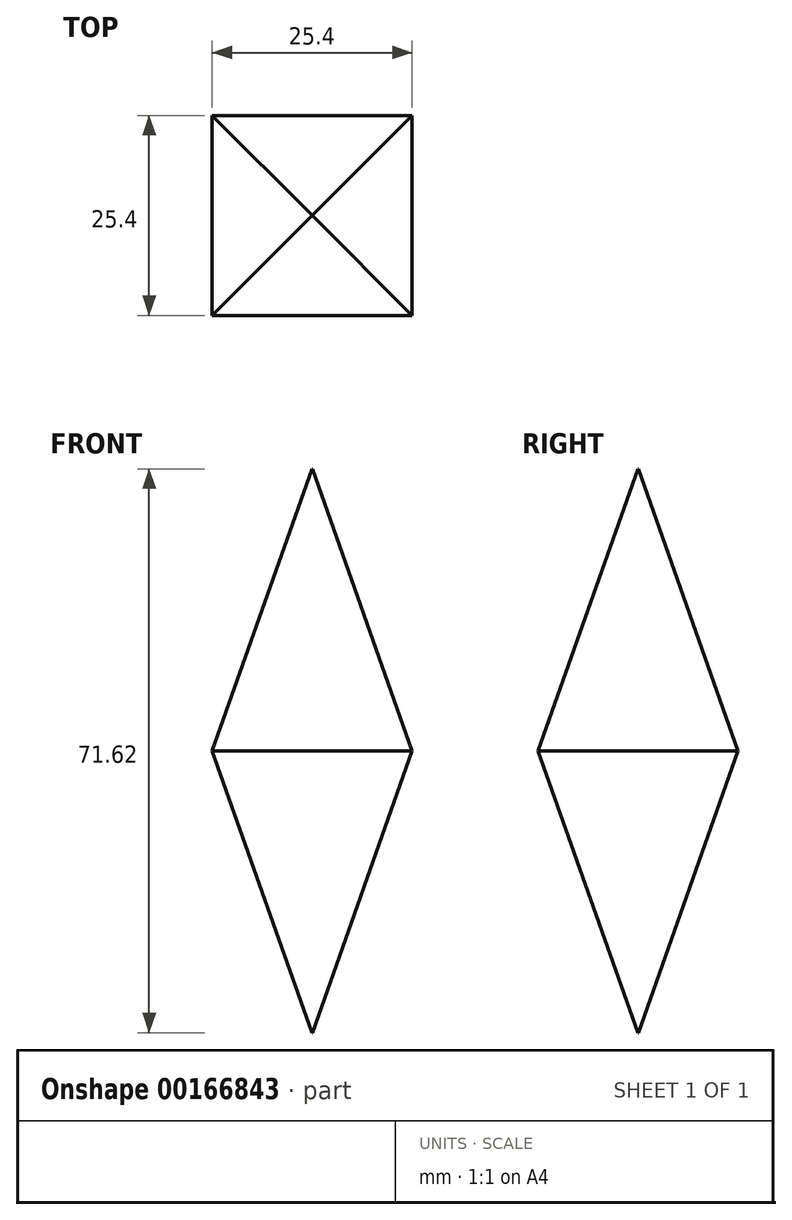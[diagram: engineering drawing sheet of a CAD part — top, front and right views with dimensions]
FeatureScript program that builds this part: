
annotation { "Feature Type Name" : "Feature", "Feature Type Description" : "" }
export const myFeature = defineFeature(function(context is Context, id is Id, definition is map)
    precondition{}
    {
        {
            var Q0;
            Q0=qCreatedBy(makeId("Top.planeOp"),FACE);
            var sketch = newSketch(context, id + "F0", { "sketchPlane" : qUnion([Q0])});
            skLineSegment(sketch, "E0.bottom", {"start": v(12.7, 12.7) * mm, "end": v(-12.7, 12.7) * mm});
            skLineSegment(sketch, "E0.top", {"start": v(12.7, -12.7) * mm, "end": v(-12.7, -12.7) * mm});
            skLineSegment(sketch, "E0.left", {"start": v(12.7, 12.7) * mm, "end": v(12.7, -12.7) * mm});
            skLineSegment(sketch, "E0.right", {"start": v(-12.7, 12.7) * mm, "end": v(-12.7, -12.7) * mm});
            skPoint(sketch, "E0.middle", {"position": v(0, 0) * mm});
            skSolve(sketch);
        }
        {
            var Q0;
            Q0=makeQuery(id+"F0.imprint","IMPRINT",FACE,{"disambiguationData":[TD([[makeQuery(id+"F0.imprint","IMPRINT",EDGE,{"derivedFrom":sQuery(id+"F0.wireOp",EDGE,"E0.bottom")}),1.0]])]});
            extrude(context, id + "F1", {"entities" : qUnion([Q0]), "depth" : 35.81 * mm, "hasDraft" : true, "draftAngle" : 19.47 * degree, "draftPullDirection" : true});
        }
        {
            var Q0;
            Q0=qCreatedBy(makeId("Top.planeOp"),FACE);
            var sketch = newSketch(context, id + "F2", { "sketchPlane" : qUnion([Q0])});
            skLineSegment(sketch, "E1.bottom", {"start": v(12.7, 12.7) * mm, "end": v(-12.7, 12.7) * mm});
            skLineSegment(sketch, "E1.top", {"start": v(12.7, -12.7) * mm, "end": v(-12.7, -12.7) * mm});
            skLineSegment(sketch, "E1.left", {"start": v(12.7, 12.7) * mm, "end": v(12.7, -12.7) * mm});
            skLineSegment(sketch, "E1.right", {"start": v(-12.7, 12.7) * mm, "end": v(-12.7, -12.7) * mm});
            skPoint(sketch, "E1.middle", {"position": v(0, 0) * mm});
            skSolve(sketch);
        }
        {
            var Q0;
            Q0=makeQuery(id+"F2.imprint","IMPRINT",FACE,{"disambiguationData":[TD([[makeQuery(id+"F2.imprint","IMPRINT",EDGE,{"derivedFrom":sQuery(id+"F2.wireOp",EDGE,"E1.bottom")}),1.0]])]});
            extrude(context, id + "F3", {"entities" : qUnion([Q0]), "operationType" : NewBodyOperationType.ADD, "oppositeDirection" : true, "depth" : 35.81 * mm, "hasDraft" : true, "draftAngle" : 19.47 * degree, "draftPullDirection" : true});
        }
    });
